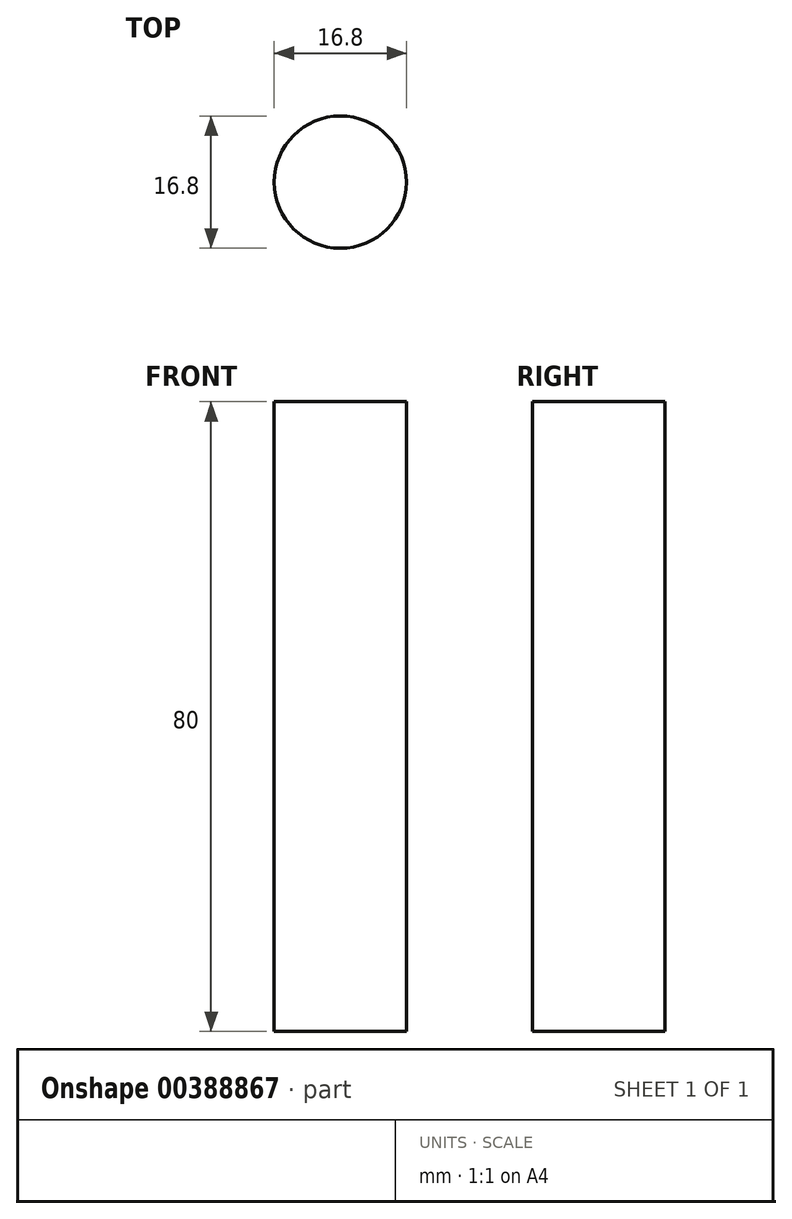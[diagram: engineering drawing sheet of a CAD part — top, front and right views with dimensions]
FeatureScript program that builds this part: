
annotation { "Feature Type Name" : "Feature", "Feature Type Description" : "" }
export const myFeature = defineFeature(function(context is Context, id is Id, definition is map)
    precondition{}
    {
        {
            var Q0;
            Q0=qCreatedBy(makeId("Top.planeOp"),FACE);
            var sketch = newSketch(context, id + "F0", { "sketchPlane" : qUnion([Q0])});
            skCircle(sketch, "E0", {"center": v(0, 0) * mm, "radius": 8.4 * mm});
            skSolve(sketch);
        }
        {
            var Q0;
            Q0 = qSketchRegion(id + "F0", true);
            extrude(context, id + "F1", {"entities" : qUnion([Q0]), "depth" : 80 * mm, "offsetDistance" : 25 * mm});
        }
    });
